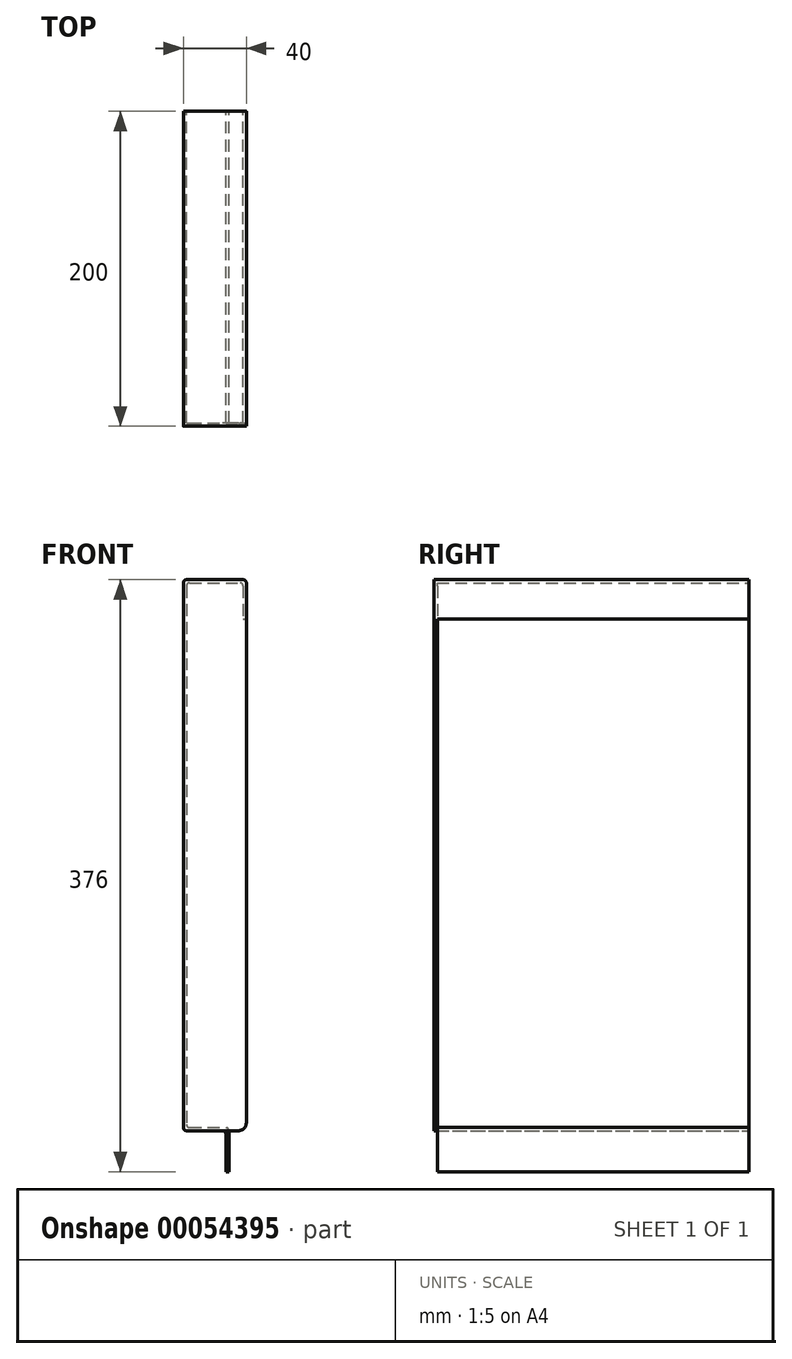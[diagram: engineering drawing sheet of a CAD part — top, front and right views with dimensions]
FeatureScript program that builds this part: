
annotation { "Feature Type Name" : "Feature", "Feature Type Description" : "" }
export const myFeature = defineFeature(function(context is Context, id is Id, definition is map)
    precondition{}
    {
        {
            var Q0;
            Q0=qCreatedBy(makeId("Front.planeOp"),FACE);
            var sketch = newSketch(context, id + "F0", { "sketchPlane" : qUnion([Q0])});
            skLineSegment(sketch, "E0", {"start": v(0, 0) * mm, "end": v(0, -350) * mm});
            skLineSegment(sketch, "E1", {"start": v(0, -350) * mm, "end": v(27, -350) * mm});
            skLineSegment(sketch, "E2", {"start": v(27, -350) * mm, "end": v(27, -376) * mm});
            skLineSegment(sketch, "E3", {"start": v(0, 0) * mm, "end": v(40, 0) * mm});
            skLineSegment(sketch, "E4", {"start": v(40, 0) * mm, "end": v(40, -25) * mm});
            skLineSegment(sketch, "E5.0", {"start": v(38, -2) * mm, "end": v(38, -25) * mm});
            skLineSegment(sketch, "E5.1", {"start": v(29, -348) * mm, "end": v(29, -376) * mm});
            skLineSegment(sketch, "E5.2", {"start": v(2, -348) * mm, "end": v(29, -348) * mm});
            skLineSegment(sketch, "E5.3", {"start": v(2, -2) * mm, "end": v(2, -348) * mm});
            skLineSegment(sketch, "E5.4", {"start": v(2, -2) * mm, "end": v(38, -2) * mm});
            skLineSegment(sketch, "E6", {"start": v(38, -25) * mm, "end": v(40, -25) * mm});
            skLineSegment(sketch, "E7", {"start": v(27, -376) * mm, "end": v(29, -376) * mm});
            skSolve(sketch);
        }
        {
            var Q0;
            Q0=qCreatedBy(makeId("Top.planeOp"),FACE);
            var sketch = newSketch(context, id + "F1", { "sketchPlane" : qUnion([Q0])});
            skLineSegment(sketch, "E8", {"start": v(0, 0) * mm, "end": v(0, 198) * mm});
            skSolve(sketch);
        }
        {
            var Q0;
            Q0=qSketchRegion(id+"F0",true);
            var Q1;
            Q1=qConstructionFilter(qBodyType(qCreatedBy(id+"F1",EDGE),BodyType.WIRE),ConstructionObject.NO);
            sweep(context, id + "F2", {"profiles" : qUnion([Q0]), "path" : qUnion([Q1])});
        }
        {
            var Q0;
            Q0=makeQuery(id+"F2.opSweep","CAP_FACE",FACE,{"disambiguationData":[OSD([sQuery(id+"F0.wireOp",EDGE,"E0"),sQuery(id+"F0.wireOp",EDGE,"E1"),sQuery(id+"F0.wireOp",EDGE,"E2"),sQuery(id+"F0.wireOp",EDGE,"E3"),sQuery(id+"F0.wireOp",EDGE,"E4"),sQuery(id+"F0.wireOp",EDGE,"E5.0"),sQuery(id+"F0.wireOp",EDGE,"E5.1"),sQuery(id+"F0.wireOp",EDGE,"E5.2"),sQuery(id+"F0.wireOp",EDGE,"E5.3"),sQuery(id+"F0.wireOp",EDGE,"E5.4"),sQuery(id+"F0.wireOp",EDGE,"E6"),sQuery(id+"F0.wireOp",EDGE,"E7"),sQuery(id+"F1.wireOp",VERTEX,"E8.start")])],"isStart":true});
            var sketch = newSketch(context, id + "F3", { "sketchPlane" : qUnion([Q0])});
            skLineSegment(sketch, "E9.0", {"start": v(40, 0) * mm, "end": v(0, 0) * mm});
            skLineSegment(sketch, "E10.0", {"start": v(0, -350) * mm, "end": v(0, 0) * mm});
            skPoint(sketch, "E11.0.end.orphan", {"position": v(27, -350) * mm});
            skPoint(sketch, "E12.0.start.orphan", {"position": v(40, -25) * mm});
            skLineSegment(sketch, "E13", {"start": v(40, 0) * mm, "end": v(40, -345) * mm});
            skLineSegment(sketch, "E14", {"start": v(35, -350) * mm, "end": v(0, -350) * mm});
            skPoint(sketch, "E15.visualSharp", {"position": v(40, -350) * mm});
            skArc(sketch, "E15.filletArc", {"start": v(35, -350) * mm, "mid": v(38.54, -348.54) * mm, "end": v(40, -345) * mm});
            skSolve(sketch);
        }
        {
            var Q0;
            Q0=qSketchRegion(id+"F3",true);
            extrude(context, id + "F4", {"entities" : qUnion([Q0]), "depth" : 2 * mm});
        }
        {
            var Q0;
            Q0=makeQuery(id+"F2.opSweep","SWEPT_BODY",BODY,{"disambiguationData":[OSD([sQuery(id+"F0.wireOp",EDGE,"E0"),sQuery(id+"F0.wireOp",EDGE,"E1"),sQuery(id+"F0.wireOp",EDGE,"E2"),sQuery(id+"F0.wireOp",EDGE,"E3"),sQuery(id+"F0.wireOp",EDGE,"E4"),sQuery(id+"F0.wireOp",EDGE,"E5.0"),sQuery(id+"F0.wireOp",EDGE,"E5.1"),sQuery(id+"F0.wireOp",EDGE,"E5.2"),sQuery(id+"F0.wireOp",EDGE,"E5.3"),sQuery(id+"F0.wireOp",EDGE,"E5.4"),sQuery(id+"F0.wireOp",EDGE,"E6"),sQuery(id+"F0.wireOp",EDGE,"E7"),sQuery(id+"F1.wireOp",EDGE,"E8")])]});
            var Q1;
            Q1=makeQuery(id+"F4.opExtrude","SWEPT_BODY",BODY,{"disambiguationData":[OSD([sQuery(id+"F3.wireOp",EDGE,"E9.0"),sQuery(id+"F3.wireOp",EDGE,"E10.0"),sQuery(id+"F3.wireOp",EDGE,"E13"),sQuery(id+"F3.wireOp",EDGE,"E14"),sQuery(id+"F3.wireOp",EDGE,"E15.filletArc")])]});
            booleanBodies(context, id + "F5", {"operationType" : BooleanOperationType.UNION, "tools" : qUnion([Q0, Q1])});
        }
        {
            var Q0;
            Q0=makeQuery(id+"F2.opSweep","SWEPT_EDGE",EDGE,{"disambiguationData":[OSD([sQuery(id+"F0.wireOp",EDGE,"E5.2"),sQuery(id+"F0.wireOp",EDGE,"E5.3"),sQuery(id+"F1.wireOp",EDGE,"E8")])]});
            var Q1;
            Q1=makeQuery(id+"F2.opSweep","SWEPT_EDGE",EDGE,{"disambiguationData":[OSD([sQuery(id+"F0.wireOp",EDGE,"E5.1"),sQuery(id+"F0.wireOp",EDGE,"E5.2"),sQuery(id+"F1.wireOp",EDGE,"E8")])]});
            var Q2;
            Q2=makeQuery(id+"F2.opSweep","SWEPT_EDGE",EDGE,{"disambiguationData":[OSD([sQuery(id+"F0.wireOp",EDGE,"E1"),sQuery(id+"F0.wireOp",EDGE,"E2"),sQuery(id+"F1.wireOp",EDGE,"E8")])]});
            var Q3;
            Q3=makeQuery(id+"F5.opBoolean","MERGE",EDGE,{"derivedFrom":[makeQuery(id+"F2.opSweep","SWEPT_EDGE",EDGE,{"disambiguationData":[OSD([sQuery(id+"F0.wireOp",EDGE,"E0"),sQuery(id+"F0.wireOp",EDGE,"E1"),sQuery(id+"F1.wireOp",EDGE,"E8")])]}),makeQuery(id+"F4.opExtrude","SWEPT_EDGE",EDGE,{"disambiguationData":[OSD([sQuery(id+"F3.wireOp",EDGE,"E10.0"),sQuery(id+"F3.wireOp",EDGE,"E14")])]})]});
            var Q4;
            Q4=makeQuery(id+"F5.opBoolean","MERGE",EDGE,{"derivedFrom":[makeQuery(id+"F2.opSweep","SWEPT_EDGE",EDGE,{"disambiguationData":[OSD([sQuery(id+"F0.wireOp",EDGE,"E3"),sQuery(id+"F0.wireOp",EDGE,"E4"),sQuery(id+"F1.wireOp",EDGE,"E8")])]}),makeQuery(id+"F4.opExtrude","SWEPT_EDGE",EDGE,{"disambiguationData":[OSD([sQuery(id+"F3.wireOp",EDGE,"E9.0"),sQuery(id+"F3.wireOp",EDGE,"E13")])]})]});
            var Q5;
            Q5=makeQuery(id+"F5.opBoolean","MERGE",EDGE,{"derivedFrom":[makeQuery(id+"F2.opSweep","SWEPT_EDGE",EDGE,{"disambiguationData":[OSD([sQuery(id+"F0.wireOp",EDGE,"E0"),sQuery(id+"F0.wireOp",EDGE,"E3"),sQuery(id+"F1.wireOp",EDGE,"E8")])]}),makeQuery(id+"F4.opExtrude","SWEPT_EDGE",EDGE,{"disambiguationData":[OSD([sQuery(id+"F3.wireOp",EDGE,"E9.0"),sQuery(id+"F3.wireOp",EDGE,"E10.0")])]})]});
            var Q6;
            Q6=makeQuery(id+"F2.opSweep","SWEPT_EDGE",EDGE,{"disambiguationData":[OSD([sQuery(id+"F0.wireOp",EDGE,"E5.3"),sQuery(id+"F0.wireOp",EDGE,"E5.4"),sQuery(id+"F1.wireOp",EDGE,"E8")])]});
            var Q7;
            Q7=makeQuery(id+"F2.opSweep","SWEPT_EDGE",EDGE,{"disambiguationData":[OSD([sQuery(id+"F0.wireOp",EDGE,"E5.0"),sQuery(id+"F0.wireOp",EDGE,"E5.4"),sQuery(id+"F1.wireOp",EDGE,"E8")])]});
            fillet(context, id + "F6", {"entities" : qUnion([Q0, Q1, Q2, Q3, Q4, Q5, Q6, Q7]), "radius" : 2 * mm, "tangentPropagation" : true, "allowEdgeOverflow" : false});
        }
    });
